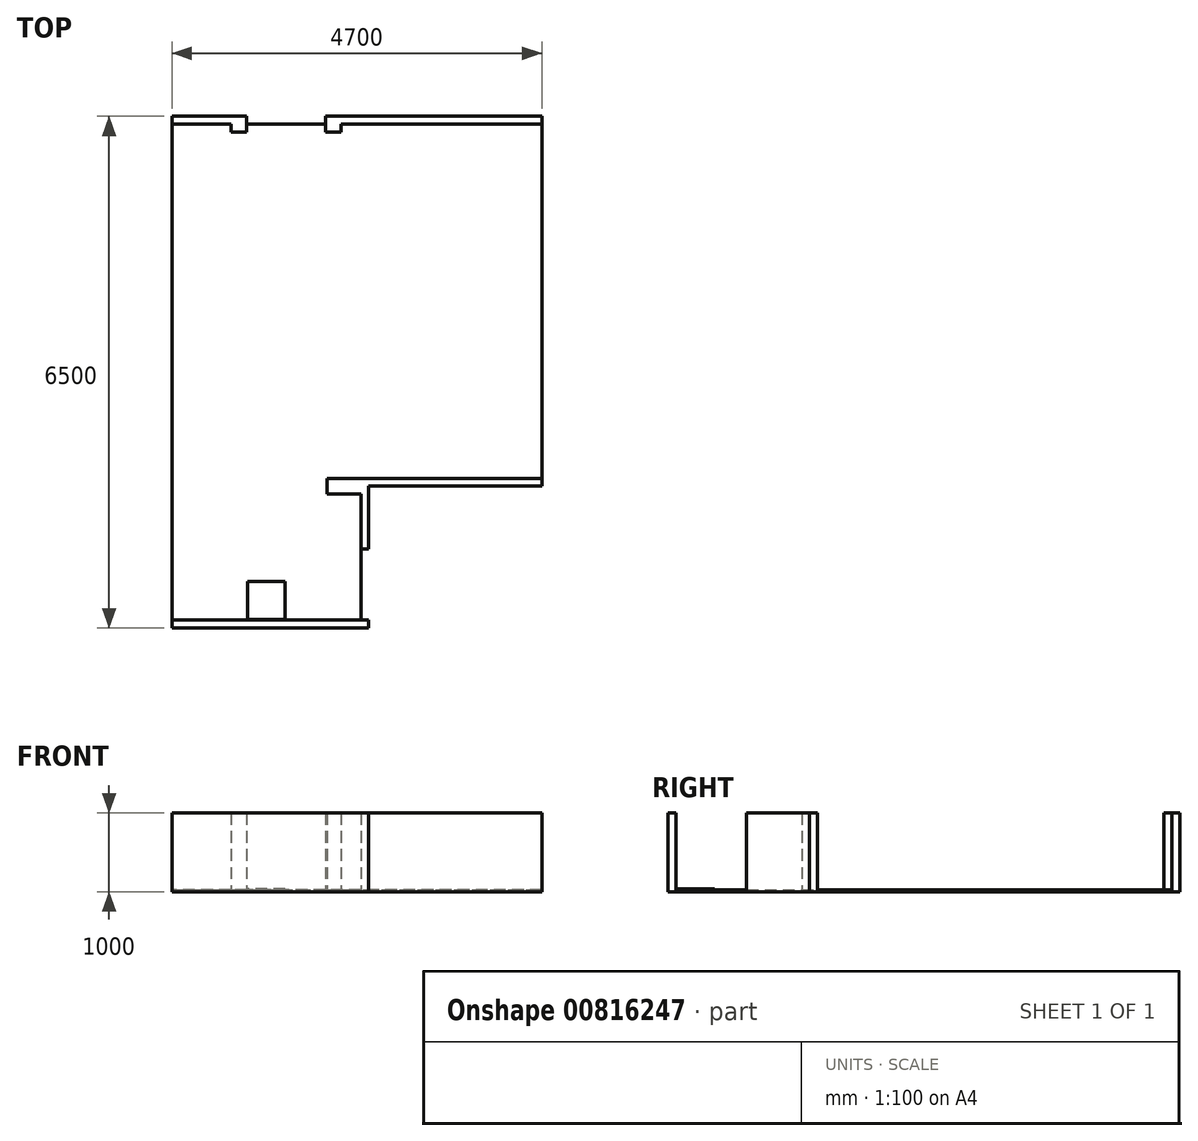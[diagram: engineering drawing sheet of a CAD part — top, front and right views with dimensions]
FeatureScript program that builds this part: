
annotation { "Feature Type Name" : "Feature", "Feature Type Description" : "" }
export const myFeature = defineFeature(function(context is Context, id is Id, definition is map)
    precondition{}
    {
        {
            var Q0;
            Q0=qCreatedBy(makeId("Top.planeOp"),FACE);
            var sketch = newSketch(context, id + "F0", { "sketchPlane" : qUnion([Q0])});
            skLineSegment(sketch, "E0", {"start": v(0, 0) * mm, "end": v(2400, 0) * mm});
            skLineSegment(sketch, "E1", {"start": v(2400, 0) * mm, "end": v(2400, 1600) * mm});
            skLineSegment(sketch, "E2", {"start": v(2400, 1600) * mm, "end": v(1970, 1600) * mm});
            skLineSegment(sketch, "E3", {"start": v(1970, 1600) * mm, "end": v(1970, 1800) * mm});
            skLineSegment(sketch, "E4", {"start": v(1970, 1800) * mm, "end": v(4700, 1800) * mm});
            skLineSegment(sketch, "E5", {"start": v(4700, 1800) * mm, "end": v(4700, 6300) * mm});
            skLineSegment(sketch, "E6", {"start": v(4700, 6300) * mm, "end": v(0, 6300) * mm});
            skLineSegment(sketch, "E7", {"start": v(0, 6300) * mm, "end": v(0, 0) * mm});
            skSolve(sketch);
        }
        {
            var Q0;
            Q0=qCreatedBy(makeId("Top.planeOp"),FACE);
            var sketch = newSketch(context, id + "F1", { "sketchPlane" : qUnion([Q0])});
            skLineSegment(sketch, "E8", {"start": v(0, 6300) * mm, "end": v(0, 6400) * mm});
            skLineSegment(sketch, "E9", {"start": v(0, 6400) * mm, "end": v(950, 6400) * mm});
            skLineSegment(sketch, "E10", {"start": v(950, 6400) * mm, "end": v(950, 6200) * mm});
            skLineSegment(sketch, "E11", {"start": v(950, 6200) * mm, "end": v(750, 6200) * mm});
            skLineSegment(sketch, "E12", {"start": v(750, 6200) * mm, "end": v(750, 6300) * mm});
            skLineSegment(sketch, "E13", {"start": v(750, 6300) * mm, "end": v(0, 6300) * mm});
            skSolve(sketch);
        }
        {
            var Q0;
            Q0 = qSketchRegion(id + "F1", true);
            extrude(context, id + "F2", {"entities" : qUnion([Q0]), "depth" : 1000 * mm, "offsetDistance" : 25 * mm});
        }
        {
            var Q0;
            Q0=qCreatedBy(makeId("Top.planeOp"),FACE);
            var sketch = newSketch(context, id + "F3", { "sketchPlane" : qUnion([Q0])});
            skLineSegment(sketch, "E14", {"start": v(4700, 6400) * mm, "end": v(1950, 6400) * mm});
            skLineSegment(sketch, "E15", {"start": v(1950, 6400) * mm, "end": v(1950, 6200) * mm});
            skLineSegment(sketch, "E16", {"start": v(1950, 6200) * mm, "end": v(2150, 6200) * mm});
            skLineSegment(sketch, "E17", {"start": v(2150, 6200) * mm, "end": v(2150, 6300) * mm});
            skLineSegment(sketch, "E18", {"start": v(2150, 6300) * mm, "end": v(4700, 6300) * mm});
            skLineSegment(sketch, "E19", {"start": v(4700, 6300) * mm, "end": v(4700, 6400) * mm});
            skSolve(sketch);
        }
        {
            var Q0;
            Q0 = qSketchRegion(id + "F3", true);
            extrude(context, id + "F4", {"entities" : qUnion([Q0]), "depth" : 1000 * mm, "offsetDistance" : 25 * mm});
        }
        {
            var Q0;
            Q0=qCreatedBy(makeId("Top.planeOp"),FACE);
            var sketch = newSketch(context, id + "F5", { "sketchPlane" : qUnion([Q0])});
            skLineSegment(sketch, "E20.bottom", {"start": v(0, 0) * mm, "end": v(2500, 0) * mm});
            skLineSegment(sketch, "E20.top", {"start": v(0, -100) * mm, "end": v(2500, -100) * mm});
            skLineSegment(sketch, "E20.left", {"start": v(0, 0) * mm, "end": v(0, -100) * mm});
            skLineSegment(sketch, "E20.right", {"start": v(2500, 0) * mm, "end": v(2500, -100) * mm});
            skSolve(sketch);
        }
        {
            var Q0;
            Q0 = qSketchRegion(id + "F5", true);
            extrude(context, id + "F6", {"entities" : qUnion([Q0]), "depth" : 1000 * mm, "offsetDistance" : 25 * mm});
        }
        {
            var Q0;
            Q0=qCreatedBy(makeId("Top.planeOp"),FACE);
            var sketch = newSketch(context, id + "F7", { "sketchPlane" : qUnion([Q0])});
            skLineSegment(sketch, "E21.0", {"start": v(1970, 1800) * mm, "end": v(4700, 1800) * mm});
            skLineSegment(sketch, "E22.0", {"start": v(1970, 1600) * mm, "end": v(1970, 1800) * mm});
            skLineSegment(sketch, "E23.0", {"start": v(2400, 1600) * mm, "end": v(1970, 1600) * mm});
            skLineSegment(sketch, "E24.0", {"start": v(2400, 900) * mm, "end": v(2400, 1600) * mm});
            skLineSegment(sketch, "E25.0", {"start": v(2500, 1700) * mm, "end": v(4700, 1700) * mm});
            skLineSegment(sketch, "E25.3", {"start": v(2500, 900) * mm, "end": v(2500, 1700) * mm});
            skLineSegment(sketch, "E26", {"start": v(4700, 1800) * mm, "end": v(4700, 1700) * mm});
            skLineSegment(sketch, "E27", {"start": v(2500, 900) * mm, "end": v(2400, 900) * mm});
            skSolve(sketch);
        }
        {
            var Q0;
            Q0 = qSketchRegion(id + "F7", true);
            extrude(context, id + "F8", {"entities" : qUnion([Q0]), "depth" : 1000 * mm, "offsetDistance" : 25 * mm});
        }
        {
            var Q0;
            Q0 = qSketchRegion(id + "F0", true);
            extrude(context, id + "F9", {"entities" : qUnion([Q0]), "operationType" : NewBodyOperationType.ADD, "depth" : 25 * mm, "offsetDistance" : 25 * mm});
        }
        {
            var Q0;
            Q0=makeQuery(id+"F9.opExtrude","CAP_FACE",FACE,{"disambiguationData":[OSD([sQuery(id+"F0.wireOp",EDGE,"E0"),sQuery(id+"F0.wireOp",EDGE,"E1"),sQuery(id+"F0.wireOp",EDGE,"E2"),sQuery(id+"F0.wireOp",EDGE,"E3"),sQuery(id+"F0.wireOp",EDGE,"E4"),sQuery(id+"F0.wireOp",EDGE,"E5"),sQuery(id+"F0.wireOp",EDGE,"E6"),sQuery(id+"F0.wireOp",EDGE,"E7")])],"isStart":false});
            var sketch = newSketch(context, id + "F10", { "sketchPlane" : qUnion([Q0])});
            skLineSegment(sketch, "E28", {"start": v(1450, 6300) * mm, "end": v(1450, 0) * mm, "construction": true});
            skLineSegment(sketch, "E29.bottom", {"start": v(1440, 10) * mm, "end": v(960, 10) * mm});
            skLineSegment(sketch, "E29.top", {"start": v(1440, 490) * mm, "end": v(960, 490) * mm});
            skLineSegment(sketch, "E29.left", {"start": v(1440, 10) * mm, "end": v(1440, 490) * mm});
            skLineSegment(sketch, "E29.right", {"start": v(960, 10) * mm, "end": v(960, 490) * mm});
            skSolve(sketch);
        }
        {
            var Q0;
            Q0 = qSketchRegion(id + "F10", true);
            extrude(context, id + "F11", {"entities" : qUnion([Q0]), "operationType" : NewBodyOperationType.ADD, "depth" : 10 * mm, "offsetDistance" : 25 * mm});
        }
    });
